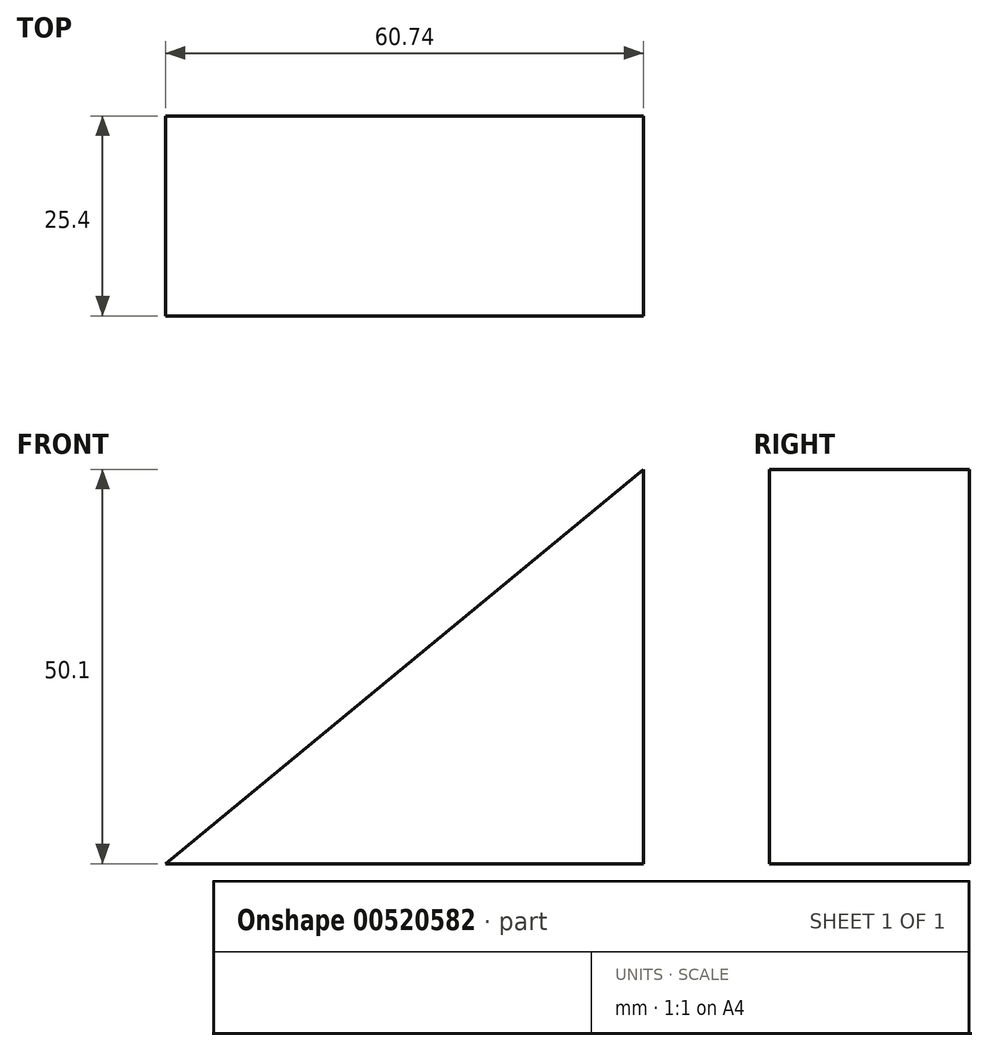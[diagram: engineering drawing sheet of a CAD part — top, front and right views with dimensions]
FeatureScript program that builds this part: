
annotation { "Feature Type Name" : "Feature", "Feature Type Description" : "" }
export const myFeature = defineFeature(function(context is Context, id is Id, definition is map)
    precondition{}
    {
        {
            var Q0;
            Q0=qCreatedBy(makeId("Front.planeOp"),FACE);
            var sketch = newSketch(context, id + "F0", { "sketchPlane" : qUnion([Q0])});
            skLineSegment(sketch, "E0", {"start": v(0, 0) * mm, "end": v(60.74, 0) * mm});
            skLineSegment(sketch, "E1", {"start": v(60.74, 0) * mm, "end": v(60.74, 50.1) * mm});
            skLineSegment(sketch, "E2", {"start": v(60.74, 50.1) * mm, "end": v(0, 0) * mm});
            skSolve(sketch);
        }
        {
            var Q0;
            Q0=makeQuery(id+"F0.imprint","IMPRINT",FACE,{"disambiguationData":[TD([[makeQuery(id+"F0.imprint","IMPRINT",EDGE,{"derivedFrom":sQuery(id+"F0.wireOp",EDGE,"E0")}),1.0]])]});
            extrude(context, id + "F1", {"entities" : qUnion([Q0]), "depth" : 25.4 * mm, "offsetDistance" : 25.4 * mm});
        }
    });
